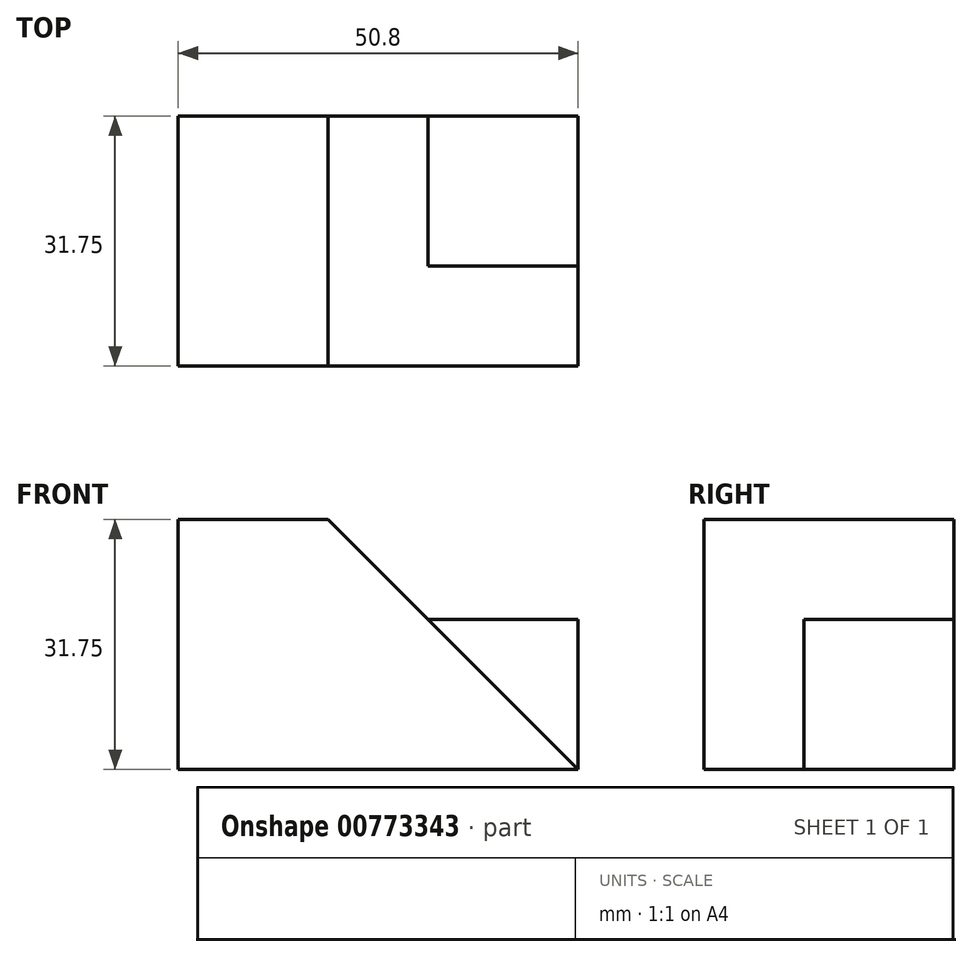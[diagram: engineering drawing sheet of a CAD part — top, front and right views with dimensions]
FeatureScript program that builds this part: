
annotation { "Feature Type Name" : "Feature", "Feature Type Description" : "" }
export const myFeature = defineFeature(function(context is Context, id is Id, definition is map)
    precondition{}
    {
        {
            var Q0;
            Q0=qCreatedBy(makeId("Front.planeOp"),FACE);
            var sketch = newSketch(context, id + "F0", { "sketchPlane" : qUnion([Q0])});
            skLineSegment(sketch, "E0", {"start": v(0, 0) * mm, "end": v(50.8, 0) * mm});
            skLineSegment(sketch, "E1", {"start": v(0, 0) * mm, "end": v(0, 31.75) * mm});
            skLineSegment(sketch, "E2", {"start": v(0, 31.75) * mm, "end": v(19.05, 31.75) * mm});
            skLineSegment(sketch, "E3", {"start": v(50.8, 0) * mm, "end": v(50.8, 19.05) * mm});
            skLineSegment(sketch, "E4", {"start": v(50.8, 19.05) * mm, "end": v(31.75, 19.05) * mm});
            skLineSegment(sketch, "E5", {"start": v(31.75, 19.05) * mm, "end": v(19.05, 31.75) * mm});
            skSolve(sketch);
        }
        {
            var Q0;
            Q0 = qSketchRegion(id + "F0", true);
            extrude(context, id + "F1", {"entities" : qUnion([Q0]), "depth" : 31.75 * mm, "offsetDistance" : 25.4 * mm});
        }
        {
            var Q0;
            Q0=makeQuery(id+"F1.opExtrude","CAP_FACE",FACE,{"disambiguationData":[OSD([sQuery(id+"F0.wireOp",EDGE,"E0"),sQuery(id+"F0.wireOp",EDGE,"E1"),sQuery(id+"F0.wireOp",EDGE,"E2"),sQuery(id+"F0.wireOp",EDGE,"E3"),sQuery(id+"F0.wireOp",EDGE,"E4"),sQuery(id+"F0.wireOp",EDGE,"E5")])],"isStart":false});
            var sketch = newSketch(context, id + "F2", { "sketchPlane" : qUnion([Q0])});
            skLineSegment(sketch, "E6", {"start": v(31.75, 19.05) * mm, "end": v(50.8, 0) * mm});
            skSolve(sketch);
        }
        {
            var Q0;
            Q0 = qSketchRegion(id + "F2", true);
            var Q1;
            Q1=makeQuery(id+"F2.imprint","IMPRINT",FACE,{"disambiguationData":[TD([[makeQuery(id+"F2.imprint","IMPRINT",EDGE,{"derivedFrom":sQuery(id+"F2.wireOp",EDGE,"E6")}),1.0]])]});
            extrude(context, id + "F3", {"entities" : qUnion([Q0, Q1]), "operationType" : NewBodyOperationType.REMOVE, "oppositeDirection" : true, "depth" : 12.7 * mm, "offsetDistance" : 25.4 * mm});
        }
    });
